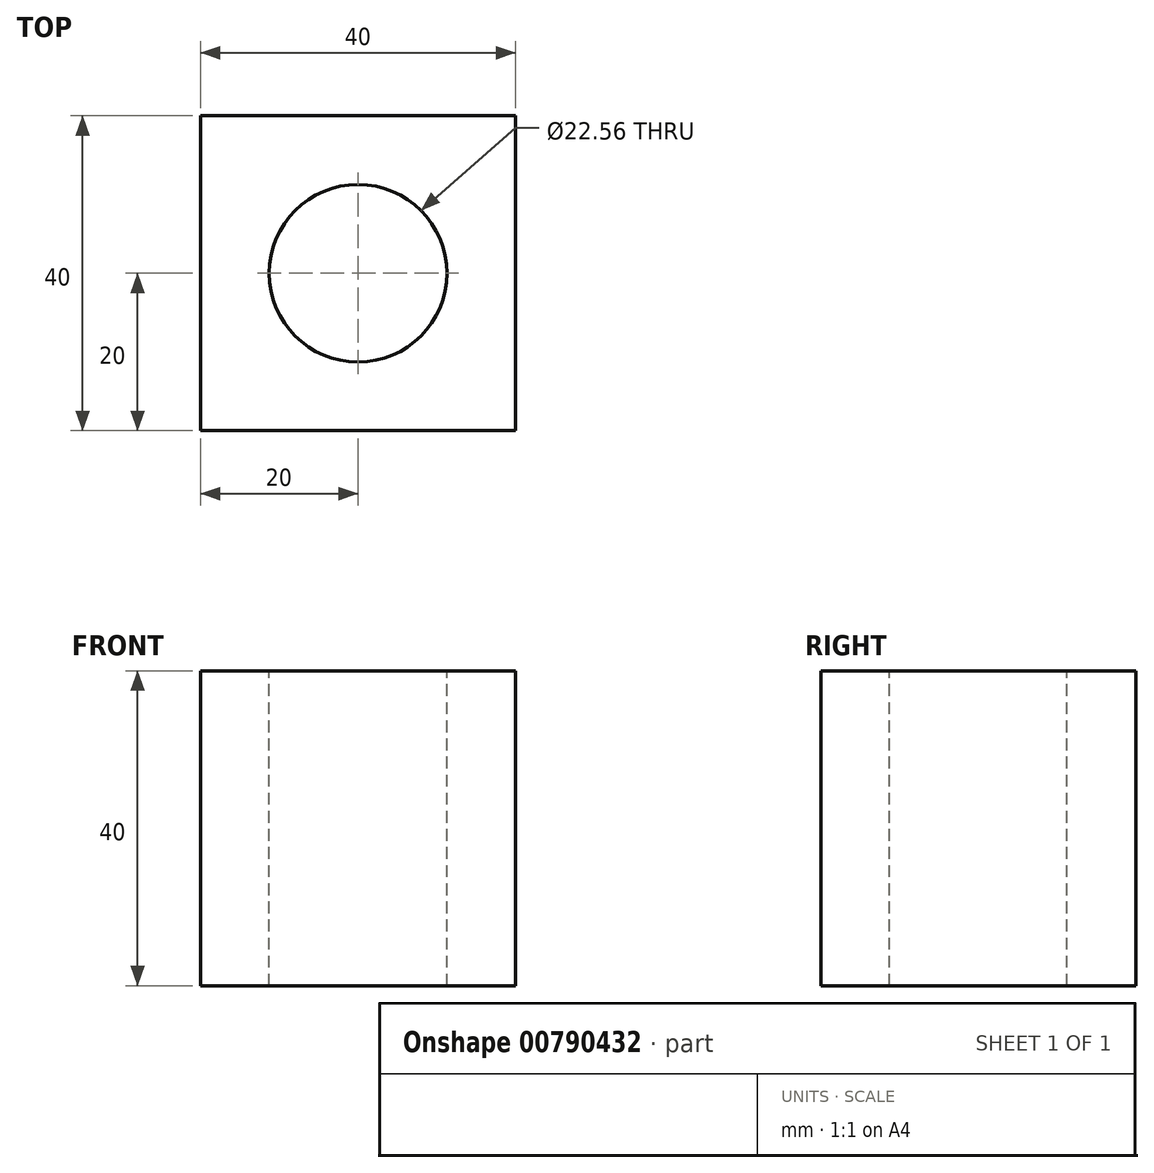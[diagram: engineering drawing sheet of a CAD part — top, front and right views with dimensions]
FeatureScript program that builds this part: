
annotation { "Feature Type Name" : "Feature", "Feature Type Description" : "" }
export const myFeature = defineFeature(function(context is Context, id is Id, definition is map)
    precondition{}
    {
        {
            var Q0;
            Q0=qCreatedBy(makeId("Front.planeOp"),FACE);
            var sketch = newSketch(context, id + "F0", { "sketchPlane" : qUnion([Q0])});
            skLineSegment(sketch, "E0.bottom", {"start": v(0, 0) * mm, "end": v(40, 0) * mm});
            skLineSegment(sketch, "E0.top", {"start": v(0, 40) * mm, "end": v(40, 40) * mm});
            skLineSegment(sketch, "E0.left", {"start": v(0, 0) * mm, "end": v(0, 40) * mm});
            skLineSegment(sketch, "E0.right", {"start": v(40, 0) * mm, "end": v(40, 40) * mm});
            skSolve(sketch);
        }
        {
            var Q0;
            Q0 = qSketchRegion(id + "F0", true);
            extrude(context, id + "F1", {"entities" : qUnion([Q0]), "depth" : 40 * mm, "offsetDistance" : 25 * mm});
        }
        {
            var Q0;
            Q0=makeQuery(id+"F1.opExtrude","SWEPT_FACE",FACE,{"disambiguationData":[OSD([sQuery(id+"F0.wireOp",EDGE,"E0.top")])]});
            var sketch = newSketch(context, id + "F2", { "sketchPlane" : qUnion([Q0])});
            skCircle(sketch, "E1", {"center": v(20, -20) * mm, "radius": 11.28 * mm});
            skPoint(sketch, "E1.centerSnap0", {"position": v(20, -40) * mm});
            skPoint(sketch, "E1.centerSnap1", {"position": v(40, -20) * mm});
            skSolve(sketch);
        }
        {
            var Q0;
            Q0=makeQuery(id+"F2.imprint","IMPRINT",FACE,{"disambiguationData":[TD([[makeQuery(id+"F2.imprint","IMPRINT",EDGE,{"derivedFrom":sQuery(id+"F2.wireOp",EDGE,"E1")}),1.0]])]});
            var sketch = newSketch(context, id + "F3", { "sketchPlane" : qUnion([Q0])});
            skSolve(sketch);
        }
        {
            var Q0;
            Q0=makeQuery(id+"F3.imprint","IMPRINT",FACE,{"disambiguationData":[TD([[makeQuery(id+"F3.imprint","IMPRINT",EDGE,{"derivedFrom":makeQuery(id+"F2.imprint","IMPRINT",EDGE,{"derivedFrom":sQuery(id+"F2.wireOp",EDGE,"E1")})}),1.0]])]});
            extrude(context, id + "F4", {"entities" : qUnion([Q0]), "operationType" : NewBodyOperationType.REMOVE, "oppositeDirection" : true, "depth" : 40 * mm, "offsetDistance" : 25 * mm});
        }
        {
            var Q0;
            Q0=makeQuery(id+"F1.opExtrude","SWEPT_FACE",FACE,{"disambiguationData":[OSD([sQuery(id+"F0.wireOp",EDGE,"E0.left")])]});
            var sketch = newSketch(context, id + "F5", { "sketchPlane" : qUnion([Q0])});
            skLineSegment(sketch, "E2", {"start": v(20, 28.97) * mm, "end": v(20, 10.58) * mm});
            skPoint(sketch, "E2.startSnap0", {"position": v(20, 40) * mm});
            skPoint(sketch, "E2.endSnap0", {"position": v(20, 0) * mm});
            skArc(sketch, "E3", {"start": v(20, 10.58) * mm, "mid": v(29.17, 19.77) * mm, "end": v(20, 28.97) * mm});
            skSolve(sketch);
        }
        {
            var Q0;
            Q0=sQuery(id+"F5.wireOp",EDGE,"E3");
            var Q1;
            Q1=sQuery(id+"F5.wireOp",EDGE,"E2");
            revolve(context, id + "F6", {"bodyType" : ToolBodyType.SURFACE, "surfaceOperationType" : NewSurfaceOperationType.NEW, "surfaceEntities" : qUnion([Q0]), "axis" : qUnion([Q1]), "revolveType" : RevolveType.FULL});
        }
    });
